# Revit family: Haworth_CabanaLounge_SingleCollaborativeSofa_OneArm_AP_PRELIMINARY
name_source: partatom
category: Furniture
revit_build: Autodesk Revit 2018 (Build: 20170223_1515(x64)
units: mm (PartAtom-declared; Revit-internal decimal feet)

## family parameters
Always vertical = Yes
Cut with Voids When Loaded = No
OmniClass Number = 23.40.70.14.64.21
OmniClass Title = Systems Furniture
Room Calculation Point = No
Shared = No
Work Plane-Based = No

## types (9) — shared parameters
Assembly Code = E2020200
Description = Haworth - Cabana Lounge - Single / Collaborative Sofa - One Arm
Leg Offset = 70 mm  [stored 0.229659 ft]
Manufacturer = Haworth
Model = SECBXX
Revision Number = 1
Seat Depth = 762 mm  [stored 2.5 ft]
Seat Height = 459 mm  [stored 1.50591 ft]
Size = Verify Final Dim. w/ Haworth
URL = https://www.haworth.com
URL - Product = https://www.haworth.com
Warranty = http://www.haworth.com

## per-type parameters (varying)
| type | 1S no Screen | 1S with Screen | 2S no Screen | 2S with Screen | Actual Depth | Actual Height | Actual Width | High Screen | Integrated Table Control | Low Screen | No Screen | One Seat | Screen Width | Seat Width | Two Seats | With Screen | With Top |
| Two Seats - High Screen - With Integrated Table | No | No | No | Yes | 813 mm | 1372 mm  [stored 4.50131 ft] | 1880 mm  [stored 6.16798 ft] | Yes | Yes | No | No | No | 1880 mm  [stored 6.16798 ft] | 1829 mm  [stored 6.00066 ft] | Yes | Yes | Yes |
| Two Seats - Low Screen - With Integrated Table | No | No | No | Yes | 813 mm | 1067 mm  [stored 3.50066 ft] | 1880 mm  [stored 6.16798 ft] | No | Yes | Yes | No | No | 1880 mm  [stored 6.16798 ft] | 1829 mm  [stored 6.00066 ft] | Yes | Yes | Yes |
| Two Seats - No Screen - With Integrated Table | No | No | Yes | No | 762 mm  [stored 2.5 ft] | 772 mm  [stored 2.53281 ft] | 1829 mm  [stored 6.00066 ft] | No | Yes | No | Yes | No | 1880 mm  [stored 6.16798 ft] | 1829 mm  [stored 6.00066 ft] | Yes | No | Yes |
| Two Seats - No Screen - Without Integrated Table | No | No | Yes | No | 762 mm  [stored 2.5 ft] | 772 mm  [stored 2.53281 ft] | 1829 mm  [stored 6.00066 ft] | No | No | No | Yes | No | 1880 mm  [stored 6.16798 ft] | 1829 mm  [stored 6.00066 ft] | Yes | No | No |
| Two Seats - Low Screen - Without Integrated Table | No | No | No | Yes | 813 mm | 1067 mm  [stored 3.50066 ft] | 1880 mm  [stored 6.16798 ft] | No | No | Yes | No | No | 1880 mm  [stored 6.16798 ft] | 1829 mm  [stored 6.00066 ft] | Yes | Yes | No |
| Two Seats - High Screen - Without Integrated Table | No | No | No | Yes | 813 mm | 1372 mm  [stored 4.50131 ft] | 1880 mm  [stored 6.16798 ft] | Yes | No | No | No | No | 1880 mm  [stored 6.16798 ft] | 1829 mm  [stored 6.00066 ft] | Yes | Yes | No |
| One Seat - No Screen - Without Integrated Table | Yes | No | No | No | 762 mm  [stored 2.5 ft] | 772 mm  [stored 2.53281 ft] | 914 mm  [stored 2.99869 ft] | No | No | No | Yes | Yes | 965 mm  [stored 3.16601 ft] | 914 mm  [stored 2.99869 ft] | No | No | No |
| One Seat - Low Screen - Without Integrated Table | No | Yes | No | No | 813 mm | 1067 mm  [stored 3.50066 ft] | 965 mm  [stored 3.16601 ft] | No | No | Yes | No | Yes | 965 mm  [stored 3.16601 ft] | 914 mm  [stored 2.99869 ft] | No | Yes | No |
| One Seat - High Screen - Without Integrated Table | No | Yes | No | No | 813 mm | 1372 mm  [stored 4.50131 ft] | 965 mm  [stored 3.16601 ft] | Yes | No | No | No | Yes | 965 mm  [stored 3.16601 ft] | 914 mm  [stored 2.99869 ft] | No | Yes | No |

note: [stored X ft] marks values corroborated as IEEE doubles in the binary element streams (Revit-internal decimal feet)

## geometry (parser evidence)
native form markers: Extrusion x3, Sweep x14
no freeform markers — native parametric forms only
